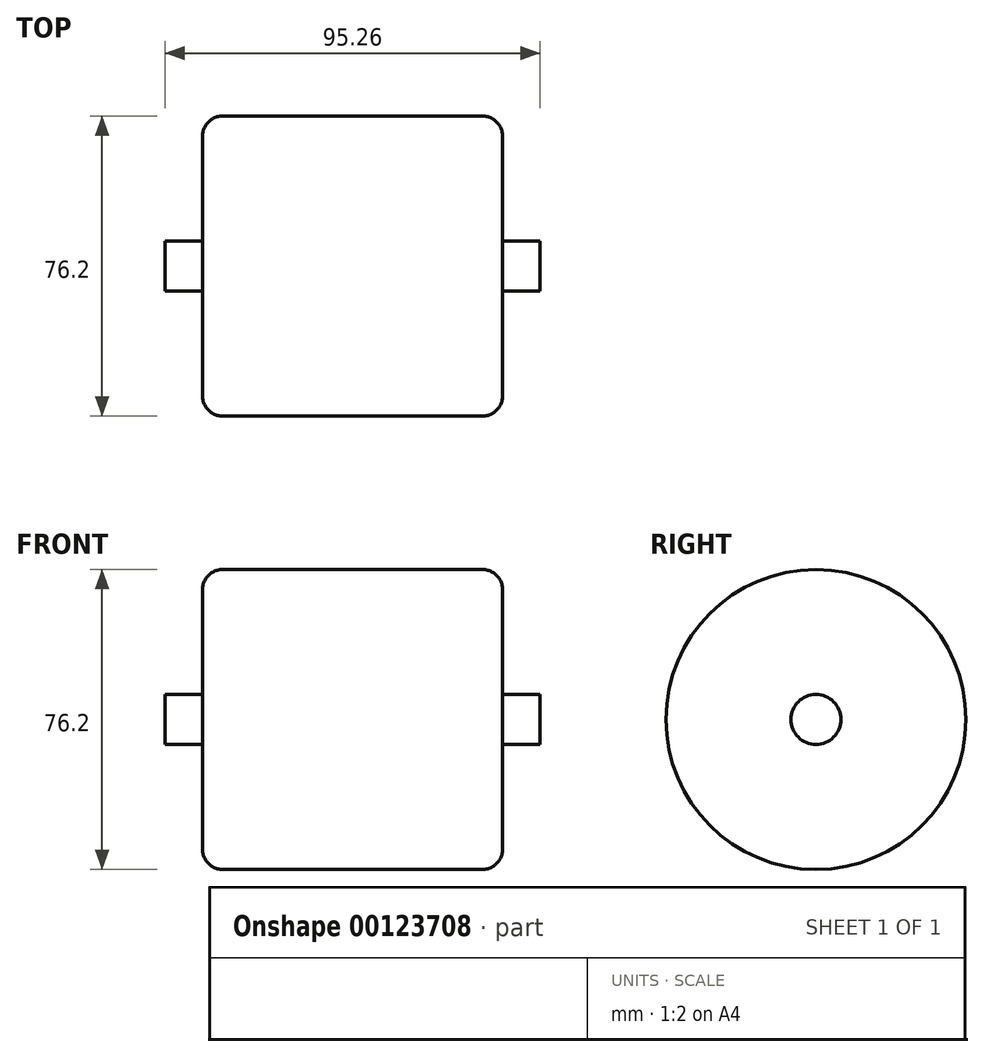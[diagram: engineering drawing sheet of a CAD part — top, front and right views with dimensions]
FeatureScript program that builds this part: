
annotation { "Feature Type Name" : "Feature", "Feature Type Description" : "" }
export const myFeature = defineFeature(function(context is Context, id is Id, definition is map)
    precondition{}
    {
        {
            var Q0;
            Q0=qCreatedBy(makeId("Right.planeOp"),FACE);
            var sketch = newSketch(context, id + "F0", { "sketchPlane" : qUnion([Q0])});
            skCircle(sketch, "E0", {"center": v(0, 0) * mm, "radius": 38.1 * mm});
            skCircle(sketch, "E1", {"center": v(0, 0) * mm, "radius": 6.35 * mm});
            skSolve(sketch);
        }
        {
            var Q0;
            Q0=makeQuery(id+"F0.imprint","IMPRINT",FACE,{"disambiguationData":[TD([[makeQuery(id+"F0.imprint","IMPRINT",EDGE,{"derivedFrom":sQuery(id+"F0.wireOp",EDGE,"E0")}),1.0]])]});
            extrude(context, id + "F1", {"entities" : qUnion([Q0]), "endBound" : BoundingType.SYMMETRIC, "depth" : 76.2 * mm});
        }
        {
            var Q0;
            Q0=makeQuery(id+"F1.opExtrude","CAP_EDGE",EDGE,{"disambiguationData":[OSD([sQuery(id+"F0.wireOp",EDGE,"E0")])],"isStart":false});
            var Q1;
            Q1=makeQuery(id+"F1.opExtrude","CAP_EDGE",EDGE,{"disambiguationData":[OSD([sQuery(id+"F0.wireOp",EDGE,"E0")])],"isStart":true});
            fillet(context, id + "F2", {"entities" : qUnion([Q0, Q1]), "radius" : 5.08 * mm, "tangentPropagation" : true, "allowEdgeOverflow" : false});
        }
        {
            var Q0;
            Q0=makeQuery(id+"F0.imprint","IMPRINT",FACE,{"disambiguationData":[TD([[makeQuery(id+"F0.imprint","IMPRINT",EDGE,{"derivedFrom":sQuery(id+"F0.wireOp",EDGE,"E1")}),1.0]])]});
            extrude(context, id + "F3", {"entities" : qUnion([Q0]), "operationType" : NewBodyOperationType.ADD, "endBound" : BoundingType.SYMMETRIC, "depth" : 95.25 * mm});
        }
    });
